FCSTD DOCUMENT  (FreeCAD 0.20R29177 +426 (Git))
Label: ASM_ExtensionDriver
License: All rights reserved
LicenseURL: http://en.wikipedia.org/wiki/All_rights_reserved
objects: App::Link×5, App::DocumentObjectGroup×3, PartDesign::CoordinateSystem×1, App::FeaturePython×1, App::Part×1
note: 1 computed .brp shape members not serialized (recipe doc carries the construction recipe); baked Part::Feature solids carry a one-line shape summary decoded from their .brp
EXTERNAL_REF file=ASM_Stepper.FCStd obj=LCS_Origin
EXTERNAL_REF file=ASM_Stepper.FCStd obj=Assembly
EXTERNAL_REF file=ASM_Stepper.FCStd obj=Stepper_LCS_mount
EXTERNAL_REF file=SerpentinePlate.FCStd obj=LCS_Origin
EXTERNAL_REF file=SerpentinePlate.FCStd obj=Assembly
EXTERNAL_REF file=TimingPulleyGT2.FCStd obj=LCS_Origin
EXTERNAL_REF file=TimingPulleyGT2.FCStd obj=Assembly
EXTERNAL_REF file=SerpentinePlate.FCStd obj=LCS_idler1
EXTERNAL_REF file=SmoothIdlerPulleyGT2.FCStd obj=LCS_Origin
EXTERNAL_REF file=SmoothIdlerPulleyGT2.FCStd obj=Assembly
EXTERNAL_REF file=SerpentinePlate.FCStd obj=LCS_idler2

FEATURE [App::DocumentObjectGroup] Parts
FEATURE [PartDesign::CoordinateSystem] LCS_Origin
  AttacherType = Attacher::AttachEngine3D
  MapMode = 2
  Support = -> [X_Axis]
FEATURE [App::FeaturePython] Variables  # WARN: FeaturePython — macro-defined, semantics opaque (R4)
  Type = App::PropertyContainer
FEATURE [App::DocumentObjectGroup] Constraints
FEATURE [App::DocumentObjectGroup] Configurations
FEATURE [App::Link] ASM_Stepper
  AttachedBy = #LCS_Origin
  AttachedTo = Parent Assembly#LCS_Origin
  LinkedObject = -> <external ASM_Stepper.FCStd>#Assembly
  SolverId = Asm4EE
  expr: Placement = LCS_Origin.Placement * AttachmentOffset * ASM_Stepper#LCS_Origin.Placement ^ -1
FEATURE [App::Link] SerpentinePlate
  AttachedBy = #LCS_Origin
  AttachedTo = ASM_Stepper#Stepper_LCS_mount
  AttachmentOffset = pos=(0,0,-3) rot=(-1,0,0;3.14159rad)
  LinkPlacement = pos=(0,-7.1e-15,30) rot=(-1,0,0;1.5708rad)
  LinkedObject = -> <external SerpentinePlate.FCStd>#Assembly
  Placement = pos=(0,-7.1e-15,30) rot=(-1,0,0;1.5708rad)
  SolverId = Asm4EE
  expr: Placement = ASM_Stepper.Placement * ASM_Stepper#Stepper_LCS_mount.Placement * AttachmentOffset * SerpentinePlate#LCS_Origin.Placement ^ -1
FEATURE [App::Link] TimingPulleyGT2
  AttachedBy = #LCS_Origin
  AttachedTo = ASM_Stepper#Stepper_LCS_mount
  AttachmentOffset = pos=(0,0,-26) rot=(0,0,1;0rad)
  LinkPlacement = pos=(0,23,30) rot=(1,0,0;1.5708rad)
  LinkedObject = -> <external TimingPulleyGT2.FCStd>#Assembly
  Placement = pos=(0,23,30) rot=(1,0,0;1.5708rad)
  SolverId = Asm4EE
  expr: Placement = ASM_Stepper.Placement * ASM_Stepper#Stepper_LCS_mount.Placement * AttachmentOffset * TimingPulleyGT2#LCS_Origin.Placement ^ -1
FEATURE [App::Link] SmoothIdlerPulleyGT2
  AttachedBy = #LCS_Origin
  AttachedTo = SerpentinePlate#LCS_idler1
  AttachmentOffset = pos=(0,0,1) rot=(0,0,1;0rad)
  LinkPlacement = pos=(16.3,8,37.5) rot=(-1,0,0;1.5708rad)
  LinkedObject = -> <external SmoothIdlerPulleyGT2.FCStd>#Assembly
  Placement = pos=(16.3,8,37.5) rot=(-1,0,0;1.5708rad)
  SolverId = Asm4EE
  expr: Placement = SerpentinePlate.Placement * SerpentinePlate#LCS_idler1.Placement * AttachmentOffset * SmoothIdlerPulleyGT2#LCS_Origin.Placement ^ -1
FEATURE [App::Link] SmoothIdlerPulleyGT003
  AttachedBy = #LCS_Origin
  AttachedTo = SerpentinePlate#LCS_idler2
  AttachmentOffset = pos=(0,0,1) rot=(0,0,1;0rad)
  LinkPlacement = pos=(-16.3,8,37.5) rot=(-1,0,0;1.5708rad)
  LinkedObject = -> <external SmoothIdlerPulleyGT2.FCStd>#Assembly
  Placement = pos=(-16.3,8,37.5) rot=(-1,0,0;1.5708rad)
  SolverId = Asm4EE
  expr: Placement = SerpentinePlate.Placement * SerpentinePlate#LCS_idler2.Placement * AttachmentOffset * SmoothIdlerPulleyGT2#LCS_Origin.Placement ^ -1
FEATURE [App::Part] Assembly
  AssemblyType = Part::Link
  Group = -> [LCS_Origin,Variables,Constraints,Configurations,ASM_Stepper,SerpentinePlate,TimingPulleyGT2,SmoothIdlerPulleyGT2,SmoothIdlerPulleyGT003]
  Origin = -> Origin
  Type = Assembly

RESOLVED EXTERNAL PARTS (link-assembly join: the EXTERNAL_REF files above that resolve inside this repo's crawl, each included once):
---- part ASM_Stepper.FCStd = doc fcstd_b44b04883d39 ----
FCSTD DOCUMENT  (FreeCAD 0.20R29177 +426 (Git))
Label: ASM_Stepper
License: All rights reserved
LicenseURL: http://en.wikipedia.org/wiki/All_rights_reserved
objects: App::DocumentObjectGroup×3, PartDesign::CoordinateSystem×2, App::Link×2, App::FeaturePython×1, App::Part×1
note: 2 computed .brp shape members not serialized (recipe doc carries the construction recipe); baked Part::Feature solids carry a one-line shape summary decoded from their .brp
EXTERNAL_REF file=MotorBracket.FCStd obj=LCS_motor_mount
EXTERNAL_REF file=Stepper17.FCStd obj=LCS_mount
EXTERNAL_REF file=Stepper17.FCStd obj=Body
EXTERNAL_REF file=MotorBracket.FCStd obj=LCS_bottom
EXTERNAL_REF file=MotorBracket.FCStd obj=Assembly

FEATURE [App::DocumentObjectGroup] Parts
FEATURE [PartDesign::CoordinateSystem] LCS_Origin
  AttacherType = Attacher::AttachEngine3D
  MapMode = 2
  Support = -> [X_Axis]
FEATURE [App::FeaturePython] Variables  # WARN: FeaturePython — macro-defined, semantics opaque (R4)
  Type = App::PropertyContainer
FEATURE [App::DocumentObjectGroup] Constraints
FEATURE [App::DocumentObjectGroup] Configurations
FEATURE [App::Link] Stepper
  AssemblyType = Part::Link
  AttachedBy = #LCS_mount
  AttachedTo = MotorBracket#LCS_motor_mount
  LinkPlacement = pos=(0,-3,30) rot=(1,0,0;1.5708rad)
  LinkedObject = -> <external Stepper17.FCStd>#Body
  Placement = pos=(0,-3,30) rot=(1,0,0;1.5708rad)
  SolverId = Asm4EE
  expr: Placement = MotorBracket.Placement * MotorBracket#LCS_motor_mount.Placement * AttachmentOffset * Stepper17#LCS_mount.Placement ^ -1
FEATURE [App::Link] MotorBracket
  AttachedBy = #LCS_bottom
  AttachedTo = Parent Assembly#LCS_Origin
  LinkedObject = -> <external MotorBracket.FCStd>#Assembly
  SolverId = Asm4EE
  expr: Placement = LCS_Origin.Placement * AttachmentOffset * MotorBracket#LCS_bottom.Placement ^ -1
FEATURE [PartDesign::CoordinateSystem] Stepper_LCS_mount
  AttachedBy = Origin
  AttacherType = Attacher::AttachEngine3D
  Placement = pos=(0,-3,30) rot=(1,0,0;1.5708rad)
  SolverId = Asm4EE
  expr: Placement = Stepper.Placement * Stepper17#LCS_mount.Placement
FEATURE [App::Part] Assembly
  AssemblyType = Part::Link
  Group = -> [LCS_Origin,Variables,Constraints,Configurations,Stepper,MotorBracket,Stepper_LCS_mount]
  Origin = -> Origin
  Type = Assembly
---- part SerpentinePlate.FCStd = doc fcstd_52ecc4b848b1 ----
FCSTD DOCUMENT  (FreeCAD 0.20R29177 +426 (Git))
Label: SerpentinePlate
License: All rights reserved
LicenseURL: http://en.wikipedia.org/wiki/All_rights_reserved
objects: Part::FeaturePython×8, App::DocumentObjectGroup×4, PartDesign::Hole×4, PartDesign::CoordinateSystem×3, Sketcher::SketchObject×3, App::FeaturePython×1, PartDesign::Pad×1, PartDesign::Body×1, App::Part×1
note: 25 computed .brp shape members not serialized (recipe doc carries the construction recipe); baked Part::Feature solids carry a one-line shape summary decoded from their .brp

FEATURE [App::DocumentObjectGroup] Parts
FEATURE [PartDesign::CoordinateSystem] LCS_Origin
  AttacherType = Attacher::AttachEngine3D
  MapMode = 2
  Support = -> [X_Axis]
FEATURE [App::FeaturePython] Variables  # WARN: FeaturePython — macro-defined, semantics opaque (R4)
  IdlerMountOffsetX = 16.3
  IdlerMountOffsetY = 7.5
  Type = App::PropertyContainer
FEATURE [App::DocumentObjectGroup] Constraints
FEATURE [App::DocumentObjectGroup] Configurations
FEATURE [Sketcher::SketchObject] Sketch
  FullyConstrained = true
  MapMode = 5
  Support = -> [XY_Plane001]
  sketch-geometry (23):
    g0: LineSegment StartX=-15.5 StartY=15.5 StartZ=0 EndX=-15.5 EndY=-15.5 EndZ=0
    g1: LineSegment StartX=-15.5 StartY=-15.5 StartZ=0 EndX=15.5 EndY=-15.5 EndZ=0
    g2: LineSegment StartX=15.5 StartY=-15.5 StartZ=0 EndX=15.5 EndY=15.5 EndZ=0
    g3: LineSegment StartX=15.5 StartY=15.5 StartZ=0 EndX=-15.5 EndY=15.5 EndZ=0
    g4: GeomPoint X=0 Y=0 Z=0
    g5: Circle CenterX=-15.5 CenterY=15.5 CenterZ=0 NormalX=0 NormalY=0 NormalZ=1 AngleXU=0 Radius=1.7
    g6: Circle CenterX=15.5 CenterY=15.5 CenterZ=0 NormalX=0 NormalY=0 NormalZ=1 AngleXU=0 Radius=1.7
    g7: Circle CenterX=15.5 CenterY=-15.5 CenterZ=0 NormalX=0 NormalY=0 NormalZ=1 AngleXU=0 Radius=1.7
    g8: Circle CenterX=-15.5 CenterY=-15.5 CenterZ=0 NormalX=0 NormalY=0 NormalZ=1 AngleXU=0 Radius=1.7
    g9: Circle CenterX=0 CenterY=0 CenterZ=0 NormalX=0 NormalY=0 NormalZ=1 AngleXU=0 Radius=11.3
    g10: Circle CenterX=0 CenterY=0 CenterZ=0 NormalX=0 NormalY=0 NormalZ=1 AngleXU=0 Radius=6.11
    g11: ArcOfCircle CenterX=-15.5 CenterY=13 CenterZ=0 NormalX=0 NormalY=0 NormalZ=1 AngleXU=0 Radius=7.5 StartAngle=1.5708 EndAngle=3.14159
    g12: LineSegment StartX=-15.5 StartY=20.5 StartZ=0 EndX=15.5 EndY=20.5 EndZ=0
    g13: ArcOfCircle CenterX=15.5 CenterY=13 CenterZ=0 NormalX=0 NormalY=0 NormalZ=1 AngleXU=0 Radius=7.5 StartAngle=1e-16 EndAngle=1.5708
    g14: LineSegment StartX=23 StartY=13 StartZ=0 EndX=23 EndY=-13 EndZ=0
    g15: ArcOfCircle CenterX=15.5 CenterY=-13 CenterZ=0 NormalX=0 NormalY=0 NormalZ=1 AngleXU=0 Radius=7.5 StartAngle=4.71239 EndAngle=6.28319
    g16: LineSegment StartX=15.5 StartY=-20.5 StartZ=0 EndX=-15.5 EndY=-20.5 EndZ=0
    g17: ArcOfCircle CenterX=-15.5 CenterY=-13 CenterZ=0 NormalX=0 NormalY=0 NormalZ=1 AngleXU=0 Radius=7.5 StartAngle=3.14159 EndAngle=4.71239
    g18: LineSegment StartX=-23 StartY=-13 StartZ=0 EndX=-23 EndY=13 EndZ=0
    g19: GeomPoint X=-23 Y=20.5 Z=0
    g20: GeomPoint X=23 Y=-20.5 Z=0
    g21: LineSegment StartX=-15.5 StartY=20.5 StartZ=0 EndX=-15.5 EndY=15.5 EndZ=0
    g22: LineSegment StartX=15.5 StartY=-20.5 StartZ=0 EndX=15.5 EndY=-15.5 EndZ=0
  constraints (52):
    c: Coincident(g0,g1)
    c: Coincident(g1,g2)
    c: Coincident(g2,g3)
    c: Coincident(g3,g0)
    c: Horizontal(g1)
    c: Horizontal(g3)
    c: Vertical(g0)
    c: Vertical(g2)
    c: Symmetric(g1,g0,g4)
    c: Coincident(g4,g-1)
    c: Coincident(g5,g0)
    c: Coincident(g6,g2)
    c: Coincident(g7,g1)
    c: Coincident(g8,g0)
    c: Equal(g3,g0)
    c: Equal(g6,g5)
    c: Equal(g5,g8)
    c: Equal(g8,g7)
    c: Diameter(g6) = 3.4
    c: Coincident(g9,g4)
    c: Diameter(g9) = 22.6
    c: Coincident(g10,g9)
    c: Diameter(g10) = 12.22
    c: DistanceX(g3,g3) = 31
    c: Tangent(g11,g12) = 1.5708
    c: Tangent(g12,g13) = 1.5708
    c: Tangent(g13,g14) = 1.5708
    c: Tangent(g14,g15) = 1.5708
    c: Tangent(g15,g16) = 1.5708
    c: Tangent(g16,g17) = 1.5708
    c: Tangent(g17,g18) = 1.5708
    c: Tangent(g18,g11) = 1.5708
    c: Horizontal(g12)
    c: Horizontal(g16)
    c: Vertical(g14)
    c: Vertical(g18)
    c: Equal(g11,g13)
    c: Equal(g13,g15)
    c: Equal(g15,g17)
    c: PointOnObject(g19,g12)
    c: PointOnObject(g19,g18)
    c: PointOnObject(g20,g14)
    c: PointOnObject(g20,g16)
    c: DistanceX(g11,g13) = 46
    c: PointOnObject(g15,g2)
    c: DistanceY(g15,g7) = 5
    c: PointOnObject(g11,g0)
    c: Coincident(g21,g11)
    c: Coincident(g21,g0)
    c: Coincident(g22,g15)
    c: Coincident(g22,g1)
    c: Equal(g22,g21)
FEATURE [Sketcher::SketchObject] Sketch001
  AttachmentOffset = pos=(16.3,-7.5,0.5) rot=(0,0,1;0rad)
  FullyConstrained = true
  MapMode = 5
  Placement = pos=(16.3,-7.5,0.5) rot=(0,0,1;0rad)
  Support = -> [XY_Plane001]
  expr: .AttachmentOffset.Base.x = <<Variables>>.IdlerMountOffsetX
  expr: .AttachmentOffset.Base.y = <<Variables>>.IdlerMountOffsetY * -1
  expr: Constraints[5] = <<Variables>>.IdlerMountOffsetX * 2
  sketch-geometry (3):
    g0: GeomPoint X=0 Y=0 Z=0
    g1: Circle CenterX=0 CenterY=0 CenterZ=0 NormalX=0 NormalY=0 NormalZ=1 AngleXU=0 Radius=2.5
    g2: Circle CenterX=-32.6 CenterY=0 CenterZ=0 NormalX=0 NormalY=0 NormalZ=1 AngleXU=0 Radius=2.5
  constraints (6):
    c: Coincident(g0,g-1)
    c: Diameter(g1) = 5
    c: Coincident(g1,g0)
    c: PointOnObject(g2,g-1)
    c: Equal(g2,g1)
    c: DistanceX(g2,g1) = 32.6
FEATURE [PartDesign::Pad] Pad
  Direction = (0,0,1)
  Length = 7
  Length2 = 10
  Profile = -> Sketch
  ReferenceAxis = -> Sketch [N_Axis]
  Type = 0
FEATURE [PartDesign::CoordinateSystem] LCS_idler1
  AttacherType = Attacher::AttachEngine3D
  AttachmentOffset = pos=(16.3,-7.5,7) rot=(0,0,1;0rad)
  MapMode = 2
  Placement = pos=(16.3,-7.5,7) rot=(0,0,1;0rad)
  Support = -> [XY_Plane001]
  expr: .AttachmentOffset.Base.x = Variables.IdlerMountOffsetX
  expr: .AttachmentOffset.Base.y = <<Variables>>.IdlerMountOffsetY * -1
  expr: .AttachmentOffset.Base.z = <<Pad>>.Length
FEATURE [PartDesign::CoordinateSystem] LCS_idler2
  AttacherType = Attacher::AttachEngine3D
  AttachmentOffset = pos=(-16.3,-7.5,7) rot=(0,0,1;0rad)
  MapMode = 2
  Placement = pos=(-16.3,-7.5,7) rot=(0,0,1;0rad)
  Support = -> [XY_Plane001]
  expr: .AttachmentOffset.Base.x = <<Variables>>.IdlerMountOffsetX * -1
  expr: .AttachmentOffset.Base.y = <<Variables>>.IdlerMountOffsetY * -1
  expr: .AttachmentOffset.Base.z = <<Pad>>.Length
FEATURE [Part::FeaturePython] Screw  label="M3x12-Screw"  # Fasteners workbench fastener (typed FeaturePython)
  Placement = pos=(-15.5,15.5,6) rot=(0,0,1;0rad)
  baseObject = -> Sketch003 [Edge1]
  diameter = 3
  invert = false
  leftHanded = false
  length = 2
  lengthCustom = 12
  matchOuter = true
  offset = 0
  thread = false
  type = 18
FEATURE [Part::FeaturePython] Screw001  label="M3x12-Screw094"  # Fasteners workbench fastener (typed FeaturePython)
  Placement = pos=(15.5,15.5,6) rot=(0,0,1;0rad)
  baseObject = -> Sketch003 [Edge2]
  diameter = 3
  invert = false
  leftHanded = false
  length = 2
  lengthCustom = 12
  matchOuter = true
  offset = 0
  thread = false
  type = 18
FEATURE [Part::FeaturePython] Screw002  label="M3x12-Screw095"  # Fasteners workbench fastener (typed FeaturePython)
  Placement = pos=(-15.5,-15.5,6) rot=(0,0,1;0rad)
  baseObject = -> Sketch003 [Edge4]
  diameter = 3
  invert = false
  leftHanded = false
  length = 2
  lengthCustom = 12
  matchOuter = true
  offset = 0
  thread = false
  type = 18
FEATURE [Part::FeaturePython] Screw003  label="M3x12-Screw096"  # Fasteners workbench fastener (typed FeaturePython)
  Placement = pos=(15.5,-15.5,6) rot=(0,0,1;0rad)
  baseObject = -> Sketch003 [Edge3]
  diameter = 3
  invert = false
  leftHanded = false
  length = 2
  lengthCustom = 12
  matchOuter = true
  offset = 0
  thread = false
  type = 18
FEATURE [Sketcher::SketchObject] Sketch003
  AttachmentOffset = pos=(0,0,6) rot=(0,0,1;0rad)
  FullyConstrained = true
  MapMode = 5
  Placement = pos=(0,0,6) rot=(0,0,1;0rad)
  Support = -> [XY_Plane001]
  expr: .AttachmentOffset.Base.z = <<Pad>>.Length - 1mm
  sketch-geometry (19):
    g0: LineSegment StartX=-15.5 StartY=15.5 StartZ=0 EndX=-15.5 EndY=-15.5 EndZ=0
    g1: LineSegment StartX=-15.5 StartY=-15.5 StartZ=0 EndX=15.5 EndY=-15.5 EndZ=0
    g2: LineSegment StartX=15.5 StartY=-15.5 StartZ=0 EndX=15.5 EndY=15.5 EndZ=0
    g3: LineSegment StartX=15.5 StartY=15.5 StartZ=0 EndX=-15.5 EndY=15.5 EndZ=0
    g4: GeomPoint X=0 Y=0 Z=0
    g5: Circle CenterX=-15.5 CenterY=15.5 CenterZ=0 NormalX=0 NormalY=0 NormalZ=1 AngleXU=0 Radius=1.7
    g6: Circle CenterX=15.5 CenterY=15.5 CenterZ=0 NormalX=0 NormalY=0 NormalZ=1 AngleXU=0 Radius=1.7
    g7: Circle CenterX=15.5 CenterY=-15.5 CenterZ=0 NormalX=0 NormalY=0 NormalZ=1 AngleXU=0 Radius=1.7
    g8: Circle CenterX=-15.5 CenterY=-15.5 CenterZ=0 NormalX=0 NormalY=0 NormalZ=1 AngleXU=0 Radius=1.7
    g9: ArcOfCircle CenterX=-15.5 CenterY=15.5 CenterZ=0 NormalX=0 NormalY=0 NormalZ=1 AngleXU=0 Radius=6 StartAngle=1.5708 EndAngle=3.14159
    g10: LineSegment StartX=-15.5 StartY=21.5 StartZ=0 EndX=15.5 EndY=21.5 EndZ=0
    g11: ArcOfCircle CenterX=15.5 CenterY=15.5 CenterZ=0 NormalX=0 NormalY=0 NormalZ=1 AngleXU=0 Radius=6 StartAngle=1e-16 EndAngle=1.5708
    g12: LineSegment StartX=21.5 StartY=15.5 StartZ=0 EndX=21.5 EndY=-13.5 EndZ=0
    g13: ArcOfCircle CenterX=15.5 CenterY=-13.5 CenterZ=0 NormalX=0 NormalY=0 NormalZ=1 AngleXU=0 Radius=6 StartAngle=4.71239 EndAngle=6.28319
    g14: LineSegment StartX=15.5 StartY=-19.5 StartZ=0 EndX=-15.5 EndY=-19.5 EndZ=0
    g15: ArcOfCircle CenterX=-15.5 CenterY=-13.5 CenterZ=0 NormalX=0 NormalY=0 NormalZ=1 AngleXU=0 Radius=6 StartAngle=3.14159 EndAngle=4.71239
    g16: LineSegment StartX=-21.5 StartY=-13.5 StartZ=0 EndX=-21.5 EndY=15.5 EndZ=0
    g17: GeomPoint X=-21.5 Y=21.5 Z=0
    g18: GeomPoint X=21.5 Y=-19.5 Z=0
  constraints (43):
    c: Coincident(g0,g1)
    c: Coincident(g1,g2)
    c: Coincident(g2,g3)
    c: Coincident(g3,g0)
    c: Horizontal(g1)
    c: Horizontal(g3)
    c: Vertical(g0)
    c: Vertical(g2)
    c: Symmetric(g1,g0,g4)
    c: Coincident(g4,g-1)
    c: Coincident(g5,g0)
    c: Coincident(g6,g2)
    c: Coincident(g7,g1)
    c: Coincident(g8,g0)
    c: Equal(g3,g0)
    c: Equal(g6,g5)
    c: Equal(g5,g8)
    c: Equal(g8,g7)
    c: Diameter(g6) = 3.4
    c: DistanceX(g3,g3) = 31
    c: Tangent(g9,g10) = 1.5708
    c: Tangent(g10,g11) = 1.5708
    c: Tangent(g11,g12) = 1.5708
    c: Tangent(g12,g13) = 1.5708
    c: Tangent(g13,g14) = 1.5708
    c: Tangent(g14,g15) = 1.5708
    c: Tangent(g15,g16) = 1.5708
    c: Tangent(g16,g9) = 1.5708
    c: Horizontal(g10)
    c: Horizontal(g14)
    c: Vertical(g12)
    c: Vertical(g16)
    c: Equal(g9,g11)
    c: Equal(g11,g13)
    c: Equal(g13,g15)
    c: PointOnObject(g17,g10)
    c: PointOnObject(g17,g16)
    c: PointOnObject(g18,g12)
    c: PointOnObject(g18,g14)
    c: Coincident(g9,g5)
    c: DistanceX(g9,g11) = 43
    c: PointOnObject(g13,g2)
    c: DistanceY(g13,g7) = 4
FEATURE [PartDesign::Hole] Hole001  label="IdlerHoleCountersink"
  BaseFeature = -> Pad
  CustomThreadClearance = 0
  Depth = 25
  DepthType = 0
  Diameter = 5.3
  DrillForDepth = false
  DrillPoint = 1
  DrillPointAngle = 118
  HoleCutCountersinkAngle = 90
  HoleCutCustomValues = false
  HoleCutDepth = 0
  HoleCutDiameter = 12.2
  HoleCutType = 7
  ModelThread = false
  Profile = -> Sketch001
  Reversed = true
  Tapered = false
  TaperedAngle = 90
  ThreadClass = 0
  ThreadDepth = 25
  ThreadDepthType = 0
  ThreadDirection = 0
  ThreadFit = 1
  ThreadSize = 13
  ThreadType = 1
  Threaded = false
  UseCustomThreadClearance = false
FEATURE [Part::FeaturePython] Screw004  label="M5x22-Screw"  # Fasteners workbench fastener (typed FeaturePython)
  Placement = pos=(16.3,-7.5,0.5) rot=(1,0,0;3.14159rad)
  baseObject = -> Sketch001 [Edge1]
  diameter = 5
  invert = true
  leftHanded = false
  length = 11
  lengthCustom = 22
  matchOuter = false
  offset = 0
  thread = false
  type = 18
FEATURE [Part::FeaturePython] Screw005  label="M5x22-Screw001"  # Fasteners workbench fastener (typed FeaturePython)
  Placement = pos=(-16.3,-7.5,0.5) rot=(1,0,0;3.14159rad)
  baseObject = -> Sketch001 [Edge2]
  diameter = 5
  invert = true
  leftHanded = false
  length = 11
  lengthCustom = 22
  matchOuter = false
  offset = 0
  thread = false
  type = 18
FEATURE [Part::FeaturePython] Nut  label="M5-Nut"  # Fasteners workbench fastener (typed FeaturePython)
  Placement = pos=(16.3,-7.5,17.5093) rot=(0,0,1;0rad)
  baseObject = -> Screw004 [Edge9]
  diameter = 3
  invert = true
  leftHanded = false
  matchOuter = false
  offset = -4.5
  thread = false
  type = 5
FEATURE [Part::FeaturePython] Nut001  label="M5-Nut001"  # Fasteners workbench fastener (typed FeaturePython)
  Placement = pos=(-16.3,-7.5,17.5093) rot=(0,0,1;0rad)
  baseObject = -> Screw005 [Edge9]
  diameter = 3
  invert = true
  leftHanded = false
  matchOuter = true
  offset = -4.5
  thread = false
  type = 5
FEATURE [App::DocumentObjectGroup] Fasteners
  Group = -> [Screw,Screw001,Screw002,Screw003,Screw004,Screw005,Nut,Nut001]
FEATURE [PartDesign::Hole] Hole002  label="IdlerHoleCounterBore"
  BaseFeature = -> Hole001
  CustomThreadClearance = 0
  Depth = 125.273
  DepthType = 1
  Diameter = 12.2
  DrillForDepth = false
  DrillPoint = 1
  DrillPointAngle = 118
  HoleCutCountersinkAngle = 90
  HoleCutCustomValues = false
  HoleCutDepth = 0
  HoleCutDiameter = 6.1
  HoleCutType = 0
  ModelThread = false
  Profile = -> Sketch001
  Tapered = false
  TaperedAngle = 90
  ThreadClass = 0
  ThreadDepth = 125.273
  ThreadDepthType = 0
  ThreadDirection = 0
  ThreadFit = 0
  ThreadSize = 0
  ThreadType = 0
  Threaded = false
  UseCustomThreadClearance = false
  expr: Diameter = <<IdlerHoleCountersink>>.HoleCutDiameter
FEATURE [PartDesign::Hole] Hole  label="StepperHoles"
  BaseFeature = -> Hole002
  CustomThreadClearance = 0
  Depth = 25
  DepthType = 0
  Diameter = 3.4
  DrillForDepth = false
  DrillPoint = 1
  DrillPointAngle = 118
  HoleCutCountersinkAngle = 90
  HoleCutCustomValues = false
  HoleCutDepth = 0
  HoleCutDiameter = 6.7
  HoleCutType = 7
  ModelThread = false
  Profile = -> Sketch003
  Tapered = false
  TaperedAngle = 90
  ThreadClass = 0
  ThreadDepth = 25
  ThreadDepthType = 0
  ThreadDirection = 0
  ThreadFit = 0
  ThreadSize = 9
  ThreadType = 1
  Threaded = false
  UseCustomThreadClearance = false
FEATURE [PartDesign::Hole] Hole003
  BaseFeature = -> Hole
  CustomThreadClearance = 0
  Depth = 125.273
  DepthType = 1
  Diameter = 6.7
  DrillForDepth = false
  DrillPoint = 1
  DrillPointAngle = 118
  HoleCutCountersinkAngle = 90
  HoleCutCustomValues = false
  HoleCutDepth = 0
  HoleCutDiameter = 6.1
  HoleCutType = 0
  ModelThread = false
  Profile = -> Sketch003
  Reversed = true
  Tapered = false
  TaperedAngle = 90
  ThreadClass = 0
  ThreadDepth = 125.273
  ThreadDepthType = 0
  ThreadDirection = 0
  ThreadFit = 0
  ThreadSize = 0
  ThreadType = 0
  Threaded = false
  UseCustomThreadClearance = false
  expr: Diameter = <<StepperHoles>>.HoleCutDiameter
FEATURE [PartDesign::Body] Body
  Group = -> [Sketch,Sketch001,Pad,Sketch003,Hole001,Hole002,Hole,Hole003]
  Origin = -> Origin001
  Tip = -> Hole003
FEATURE [App::Part] Assembly
  AssemblyType = Part::Link
  Group = -> [LCS_Origin,Variables,Constraints,Configurations,Body,LCS_idler1,LCS_idler2,Fasteners,Screw,Screw001,Screw002,Screw003,Screw004,Screw005,Nut,Nut001]
  Origin = -> Origin
  Type = Assembly
---- part SmoothIdlerPulleyGT2.FCStd = doc fcstd_959ed8b74e3e ----
FCSTD DOCUMENT  (FreeCAD 0.20R29177 +426 (Git))
Label: SmoothIdlerPulleyGT2
License: All rights reserved
LicenseURL: http://en.wikipedia.org/wiki/All_rights_reserved
objects: App::DocumentObjectGroup×3, PartDesign::CoordinateSystem×1, App::FeaturePython×1, Sketcher::SketchObject×1, PartDesign::Revolution×1, PartDesign::Body×1, App::Part×1
note: 5 computed .brp shape members not serialized (recipe doc carries the construction recipe); baked Part::Feature solids carry a one-line shape summary decoded from their .brp

FEATURE [App::DocumentObjectGroup] Parts
FEATURE [PartDesign::CoordinateSystem] LCS_Origin
  AttacherType = Attacher::AttachEngine3D
  MapMode = 2
  Support = -> [X_Axis]
FEATURE [App::FeaturePython] Variables  # WARN: FeaturePython — macro-defined, semantics opaque (R4)
  Type = App::PropertyContainer
FEATURE [App::DocumentObjectGroup] Constraints
FEATURE [App::DocumentObjectGroup] Configurations
FEATURE [Sketcher::SketchObject] Sketch
  FullyConstrained = true
  MapMode = 5
  Placement = pos=(0,0,0) rot=(1,0,0;1.5708rad)
  Support = -> [XZ_Plane001]
  sketch-geometry (8):
    g0: LineSegment StartX=2.51 StartY=0 StartZ=0 EndX=2.51 EndY=8.56 EndZ=0
    g1: LineSegment StartX=2.51 StartY=8.56 StartZ=0 EndX=9 EndY=8.56 EndZ=0
    g2: LineSegment StartX=9 StartY=8.56 StartZ=0 EndX=9 EndY=7.58 EndZ=0
    g3: LineSegment StartX=9 StartY=7.58 StartZ=0 EndX=6.045 EndY=7.58 EndZ=0
    g4: LineSegment StartX=6.045 StartY=7.58 StartZ=0 EndX=6.045 EndY=0.98 EndZ=0
    g5: LineSegment StartX=6.045 StartY=0.98 StartZ=0 EndX=9 EndY=0.98 EndZ=0
    g6: LineSegment StartX=9 StartY=0.98 StartZ=0 EndX=9 EndY=0 EndZ=0
    g7: LineSegment StartX=9 StartY=0 StartZ=0 EndX=2.51 EndY=0 EndZ=0
  constraints (24):
    c: PointOnObject(g0,g-1)
    c: Vertical(g0)
    c: Coincident(g0,g1)
    c: Horizontal(g1)
    c: Coincident(g1,g2)
    c: Coincident(g2,g3)
    c: Horizontal(g3)
    c: Coincident(g3,g4)
    c: Vertical(g4)
    c: Coincident(g4,g5)
    c: Horizontal(g5)
    c: Coincident(g5,g6)
    c: PointOnObject(g6,g-1)
    c: Vertical(g6)
    c: Coincident(g6,g7)
    c: Coincident(g7,g0)
    c: Vertical(g2)
    c: DistanceX(g-1,g3) = 6.045
    c: DistanceX(g-1,g0) = 2.51
    c: DistanceY(g4,g4) = 6.6
    c: PointOnObject(g2,g6)
    c: DistanceX(g-1,g6) = 9
    c: DistanceY(g-1,g0) = 8.56
    c: Equal(g2,g6)
FEATURE [PartDesign::Revolution] Revolution
  Angle = 360
  Axis = (0,-2e-16,1)
  Base = (0,0,0)
  Placement = pos=(0,0,0) rot=(1,0,0;1.5708rad)
  Profile = -> Sketch
  ReferenceAxis = -> Sketch [V_Axis]
  Reversed = true
FEATURE [PartDesign::Body] Body
  Group = -> [Sketch,Revolution]
  Origin = -> Origin001
  Tip = -> Revolution
FEATURE [App::Part] Assembly
  AssemblyType = Part::Link
  Group = -> [LCS_Origin,Variables,Constraints,Configurations,Body]
  Origin = -> Origin
  Type = Assembly
---- part TimingPulleyGT2.FCStd = doc fcstd_5d79afefdc93 ----
FCSTD DOCUMENT  (FreeCAD 0.20R29177 +426 (Git))
Label: TimingPulleyGT2
License: All rights reserved
LicenseURL: http://en.wikipedia.org/wiki/All_rights_reserved
objects: App::DocumentObjectGroup×3, PartDesign::CoordinateSystem×1, App::FeaturePython×1, Sketcher::SketchObject×1, PartDesign::Revolution×1, PartDesign::Body×1, App::Part×1
note: 5 computed .brp shape members not serialized (recipe doc carries the construction recipe); baked Part::Feature solids carry a one-line shape summary decoded from their .brp

FEATURE [App::DocumentObjectGroup] Parts
FEATURE [PartDesign::CoordinateSystem] LCS_Origin
  AttacherType = Attacher::AttachEngine3D
  MapMode = 2
  Support = -> [X_Axis]
FEATURE [App::FeaturePython] Variables  # WARN: FeaturePython — macro-defined, semantics opaque (R4)
  Type = App::PropertyContainer
FEATURE [App::DocumentObjectGroup] Constraints
FEATURE [App::DocumentObjectGroup] Configurations
FEATURE [Sketcher::SketchObject] Sketch
  FullyConstrained = true
  MapMode = 5
  Placement = pos=(0,0,0) rot=(1,0,0;1.5708rad)
  Support = -> [XZ_Plane001]
  sketch-geometry (8):
    g0: LineSegment StartX=2.51 StartY=0 StartZ=0 EndX=2.51 EndY=16 EndZ=0
    g1: LineSegment StartX=2.51 StartY=16 StartZ=0 EndX=8 EndY=16 EndZ=0
    g2: LineSegment StartX=8 StartY=16 StartZ=0 EndX=8 EndY=14.1 EndZ=0
    g3: LineSegment StartX=8 StartY=14.1 StartZ=0 EndX=6.11 EndY=14.1 EndZ=0
    g4: LineSegment StartX=6.11 StartY=14.1 StartZ=0 EndX=6.11 EndY=7.1 EndZ=0
    g5: LineSegment StartX=6.11 StartY=7.1 StartZ=0 EndX=8 EndY=7.1 EndZ=0
    g6: LineSegment StartX=8 StartY=7.1 StartZ=0 EndX=8 EndY=0 EndZ=0
    g7: LineSegment StartX=8 StartY=0 StartZ=0 EndX=2.51 EndY=0 EndZ=0
  constraints (24):
    c: PointOnObject(g0,g-1)
    c: Vertical(g0)
    c: Coincident(g0,g1)
    c: Horizontal(g1)
    c: Coincident(g1,g2)
    c: Coincident(g2,g3)
    c: Horizontal(g3)
    c: Coincident(g3,g4)
    c: Vertical(g4)
    c: Coincident(g4,g5)
    c: Horizontal(g5)
    c: Coincident(g5,g6)
    c: PointOnObject(g6,g-1)
    c: Vertical(g6)
    c: Coincident(g6,g7)
    c: Coincident(g7,g0)
    c: Vertical(g2)
    c: DistanceX(g-1,g3) = 6.11
    c: DistanceX(g-1,g0) = 2.51
    c: DistanceY(g4,g4) = 7
    c: PointOnObject(g2,g6)
    c: DistanceY(g6,g6) = 7.1
    c: DistanceX(g-1,g6) = 8
    c: DistanceY(g-1,g0) = 16
FEATURE [PartDesign::Revolution] Revolution
  Angle = 360
  Axis = (0,2e-16,1)
  Base = (0,0,0)
  Placement = pos=(0,0,0) rot=(1,0,0;1.5708rad)
  Profile = -> Sketch
  ReferenceAxis = -> Sketch [V_Axis]
  Reversed = true
FEATURE [PartDesign::Body] Body
  Group = -> [Sketch,Revolution]
  Origin = -> Origin001
  Tip = -> Revolution
FEATURE [App::Part] Assembly
  AssemblyType = Part::Link
  Group = -> [LCS_Origin,Variables,Constraints,Configurations,Body]
  Origin = -> Origin
  Type = Assembly
